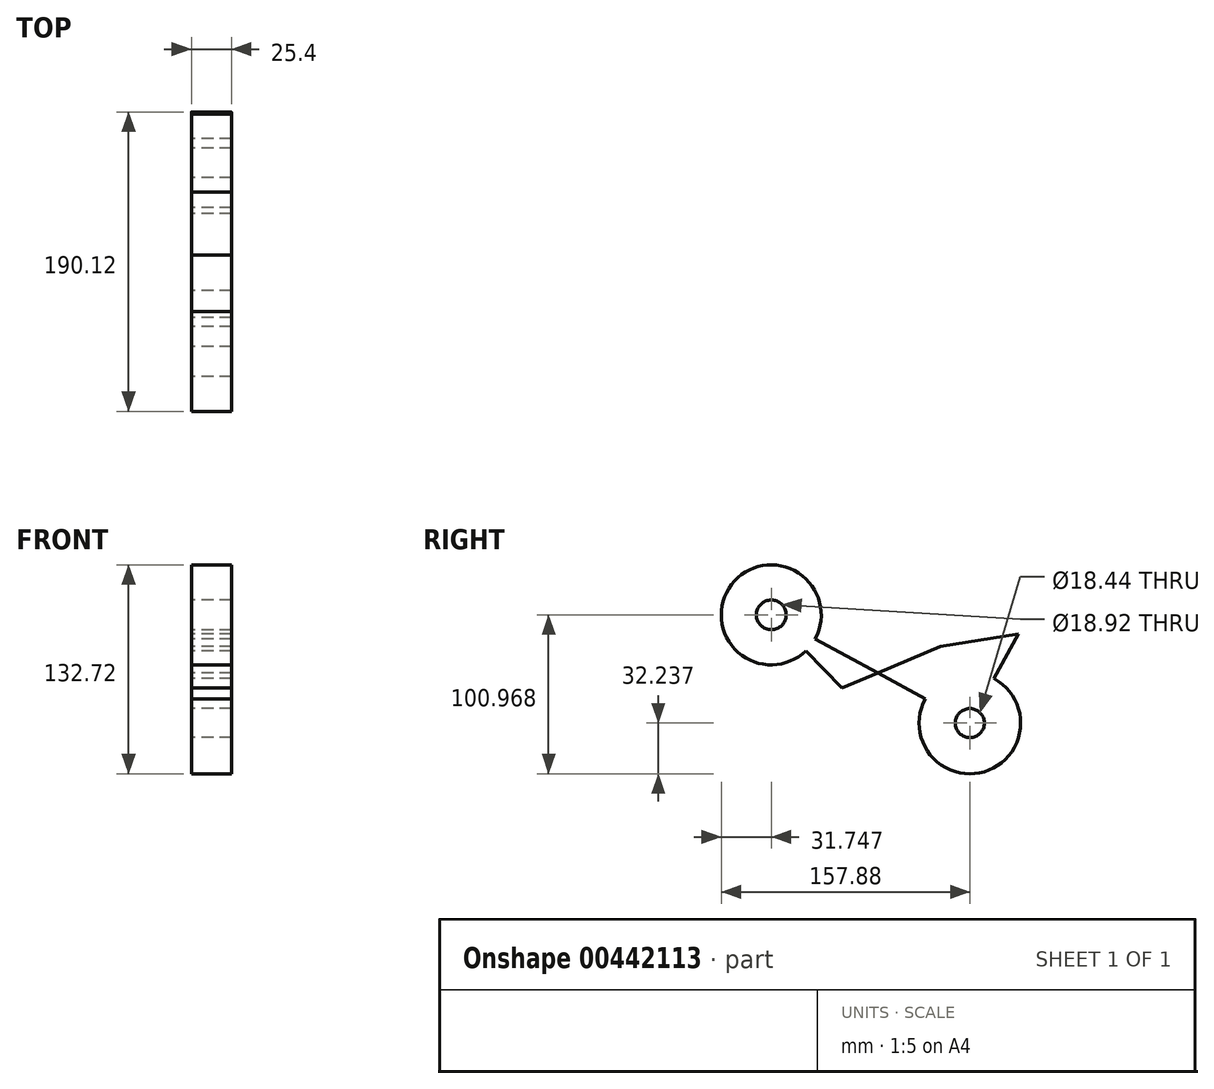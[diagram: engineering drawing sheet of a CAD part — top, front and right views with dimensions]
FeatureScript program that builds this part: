
annotation { "Feature Type Name" : "Feature", "Feature Type Description" : "" }
export const myFeature = defineFeature(function(context is Context, id is Id, definition is map)
    precondition{}
    {
        {
            var Q0;
            Q0=qCreatedBy(makeId("Right.planeOp"),FACE);
            var sketch = newSketch(context, id + "F0", { "sketchPlane" : qUnion([Q0])});
            skLineSegment(sketch, "E0", {"start": v(-79.48, 113.34) * mm, "end": v(46.65, 44.6) * mm});
            skCircle(sketch, "E1", {"center": v(-79.48, 113.34) * mm, "radius": 31.75 * mm});
            skCircle(sketch, "E2", {"center": v(46.65, 44.6) * mm, "radius": 32.24 * mm});
            skLineSegment(sketch, "E3", {"start": v(-79.48, 113.34) * mm, "end": v(-34.52, 66.79) * mm});
            skLineSegment(sketch, "E4", {"start": v(-34.52, 66.79) * mm, "end": v(27.95, 93.43) * mm});
            skLineSegment(sketch, "E5", {"start": v(-34.52, 66.79) * mm, "end": v(-8.8, 123.22) * mm});
            skLineSegment(sketch, "E6", {"start": v(46.65, 44.6) * mm, "end": v(77.46, 101.15) * mm});
            skLineSegment(sketch, "E7", {"start": v(27.95, 93.43) * mm, "end": v(77.46, 101.15) * mm});
            skCircle(sketch, "E8", {"center": v(-79.48, 113.34) * mm, "radius": 9.46 * mm});
            skCircle(sketch, "E9", {"center": v(46.65, 44.6) * mm, "radius": 9.22 * mm});
            skLineSegment(sketch, "E10", {"start": v(86.2, 89.15) * mm, "end": v(65.67, 116.9) * mm});
            skArc(sketch, "E11", {"start": v(-8.8, 123.22) * mm, "mid": v(6.44, 116.7) * mm, "end": v(0, 131.97) * mm});
            skArc(sketch, "E12", {"start": v(-12.98, 139.3) * mm, "mid": v(-12.63, 124.79) * mm, "end": v(0, 131.97) * mm});
            skSolve(sketch);
        }
        {
            var Q0;
            Q0 = qSketchRegion(id + "F0", true);
            extrude(context, id + "F1", {"entities" : qUnion([Q0]), "depth" : 25.4 * mm});
        }
    });
